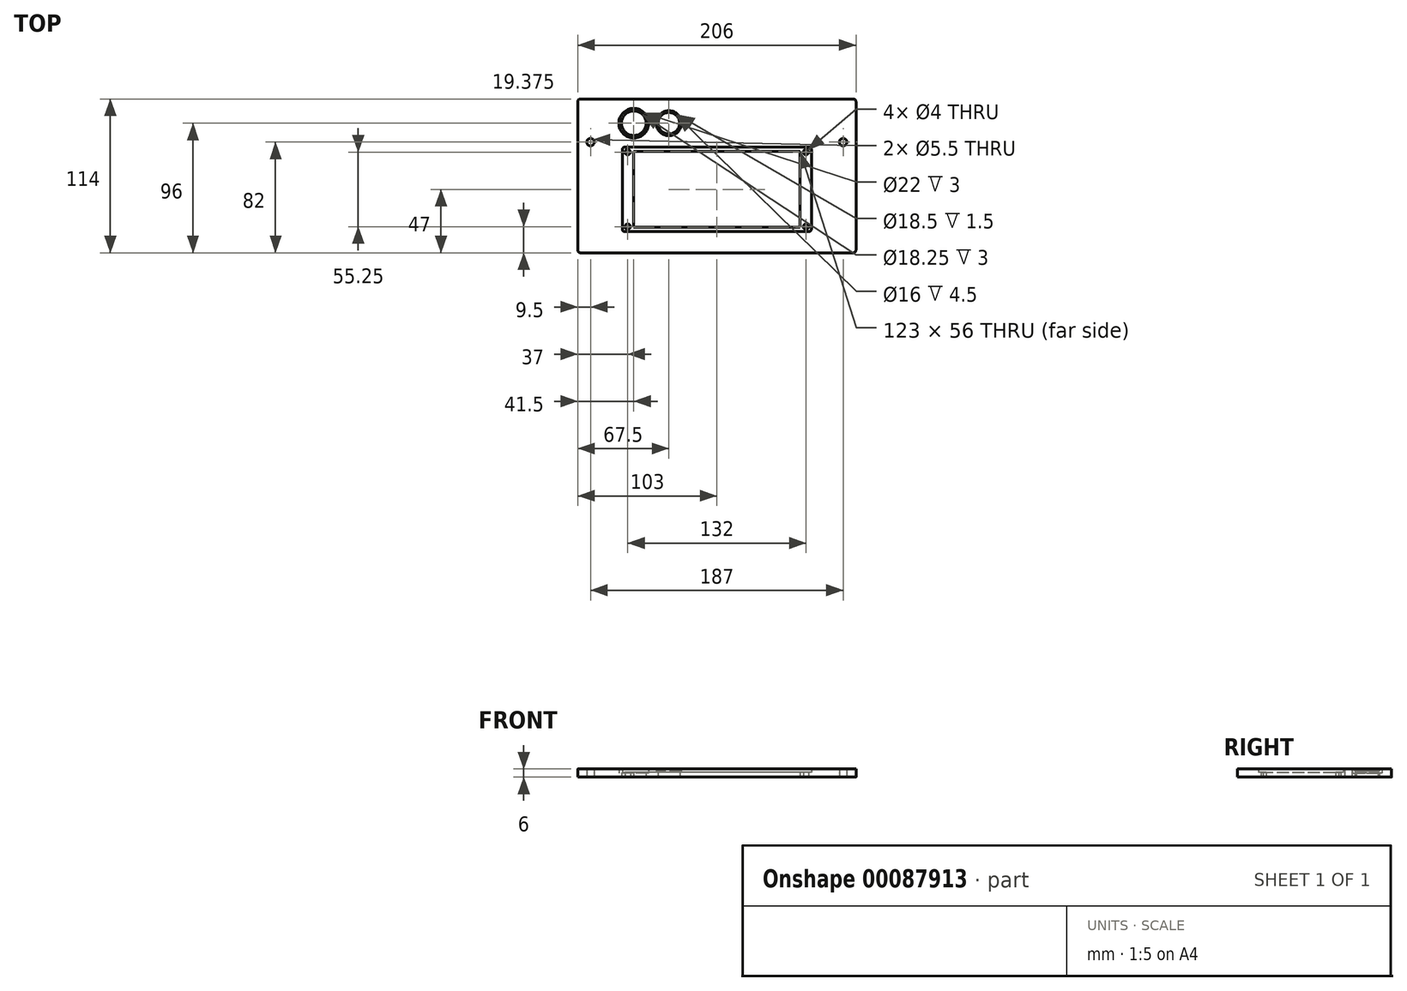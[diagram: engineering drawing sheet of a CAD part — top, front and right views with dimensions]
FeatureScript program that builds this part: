
annotation { "Feature Type Name" : "Feature", "Feature Type Description" : "" }
export const myFeature = defineFeature(function(context is Context, id is Id, definition is map)
    precondition{}
    {
        {
            var Q0;
            Q0=qCreatedBy(makeId("Top.planeOp"),FACE);
            var sketch = newSketch(context, id + "F0", { "sketchPlane" : qUnion([Q0])});
            skLineSegment(sketch, "E0.bottom", {"start": v(101, -57) * mm, "end": v(-101, -57) * mm});
            skLineSegment(sketch, "E0.top", {"start": v(101, 57) * mm, "end": v(-101, 57) * mm});
            skLineSegment(sketch, "E0.left", {"start": v(103, -55) * mm, "end": v(103, 55) * mm});
            skLineSegment(sketch, "E0.right", {"start": v(-103, -55) * mm, "end": v(-103, 55) * mm});
            skPoint(sketch, "E0.middle", {"position": v(0, 0) * mm});
            skPoint(sketch, "E1.visualSharp", {"position": v(-103, 57) * mm});
            skArc(sketch, "E1.filletArc", {"start": v(-101, 57) * mm, "mid": v(-102.41, 56.41) * mm, "end": v(-103, 55) * mm});
            skPoint(sketch, "E2.visualSharp", {"position": v(-103, -57) * mm});
            skArc(sketch, "E2.filletArc", {"start": v(-103, -55) * mm, "mid": v(-102.41, -56.41) * mm, "end": v(-101, -57) * mm});
            skPoint(sketch, "E3.visualSharp", {"position": v(103, -57) * mm});
            skArc(sketch, "E3.filletArc", {"start": v(101, -57) * mm, "mid": v(102.41, -56.41) * mm, "end": v(103, -55) * mm});
            skPoint(sketch, "E4.visualSharp", {"position": v(103, 57) * mm});
            skArc(sketch, "E4.filletArc", {"start": v(103, 55) * mm, "mid": v(102.41, 56.41) * mm, "end": v(101, 57) * mm});
            skLineSegment(sketch, "E5", {"start": v(0, 57) * mm, "end": v(0, 25) * mm, "construction": true});
            skLineSegment(sketch, "E6", {"start": v(0, 25) * mm, "end": v(93.5, 25) * mm, "construction": true});
            skCircle(sketch, "E7", {"center": v(93.5, 25) * mm, "radius": 2.75 * mm});
            skLineSegment(sketch, "E8", {"start": v(0, -57) * mm, "end": v(35.25, -57) * mm});
            skLineSegment(sketch, "E9.bottom", {"start": v(35.25, -57) * mm, "end": v(41.75, -57) * mm});
            skLineSegment(sketch, "E9.top", {"start": v(36.25, -60) * mm, "end": v(40.75, -60) * mm});
            skLineSegment(sketch, "E9.left", {"start": v(35.25, -57) * mm, "end": v(35.25, -59) * mm});
            skLineSegment(sketch, "E9.right", {"start": v(41.75, -57) * mm, "end": v(41.75, -59) * mm});
            skLineSegment(sketch, "E10", {"start": v(0, -10) * mm, "end": v(0, 0) * mm, "construction": true});
            skLineSegment(sketch, "E11.bottom", {"start": v(68, -41.38) * mm, "end": v(-68, -41.38) * mm});
            skLineSegment(sketch, "E11.top", {"start": v(68, 21.37) * mm, "end": v(-68, 21.37) * mm});
            skLineSegment(sketch, "E11.left", {"start": v(70, -39.38) * mm, "end": v(70, 19.37) * mm});
            skLineSegment(sketch, "E11.right", {"start": v(-70, -39.38) * mm, "end": v(-70, 19.37) * mm});
            skPoint(sketch, "E11.middle", {"position": v(0, -10) * mm});
            skPoint(sketch, "E12.visualSharp", {"position": v(-70, 21.37) * mm});
            skArc(sketch, "E12.filletArc", {"start": v(-68, 21.37) * mm, "mid": v(-69.41, 20.79) * mm, "end": v(-70, 19.37) * mm});
            skPoint(sketch, "E13.visualSharp", {"position": v(-70, -41.38) * mm});
            skArc(sketch, "E13.filletArc", {"start": v(-70, -39.38) * mm, "mid": v(-69.41, -40.79) * mm, "end": v(-68, -41.38) * mm});
            skPoint(sketch, "E14.visualSharp", {"position": v(70, -41.38) * mm});
            skArc(sketch, "E14.filletArc", {"start": v(68, -41.38) * mm, "mid": v(69.41, -40.79) * mm, "end": v(70, -39.38) * mm});
            skPoint(sketch, "E15.visualSharp", {"position": v(70, 21.38) * mm});
            skArc(sketch, "E15.filletArc", {"start": v(70, 19.37) * mm, "mid": v(69.41, 20.79) * mm, "end": v(68, 21.37) * mm});
            skPoint(sketch, "E16.visualSharp", {"position": v(35.25, -60) * mm});
            skArc(sketch, "E16.filletArc", {"start": v(35.25, -59) * mm, "mid": v(35.54, -59.7) * mm, "end": v(36.25, -60) * mm});
            skPoint(sketch, "E17.visualSharp", {"position": v(41.75, -60) * mm});
            skArc(sketch, "E17.filletArc", {"start": v(40.75, -60) * mm, "mid": v(41.46, -59.7) * mm, "end": v(41.75, -59) * mm});
            skCircle(sketch, "E18.MirrorC", {"center": v(-93.5, 25) * mm, "radius": 2.75 * mm});
            skLineSegment(sketch, "E19", {"start": v(66, 21.37) * mm, "end": v(66, 17.62) * mm, "construction": true});
            skLineSegment(sketch, "E20", {"start": v(66, 17.62) * mm, "end": v(0, 17.62) * mm, "construction": true});
            skCircle(sketch, "E21", {"center": v(66, 17.62) * mm, "radius": 2 * mm});
            skCircle(sketch, "E22.MirrorC", {"center": v(-66, 17.62) * mm, "radius": 2 * mm});
            skLineSegment(sketch, "E23", {"start": v(66, -41.38) * mm, "end": v(66, -37.63) * mm, "construction": true});
            skLineSegment(sketch, "E24", {"start": v(66, -37.63) * mm, "end": v(0, -37.63) * mm, "construction": true});
            skCircle(sketch, "E25", {"center": v(66, -37.63) * mm, "radius": 2 * mm});
            skCircle(sketch, "E26.MirrorC", {"center": v(-66, -37.63) * mm, "radius": 2 * mm});
            skLineSegment(sketch, "E27.MirrorCS", {"start": v(-35.25, -57) * mm, "end": v(-41.75, -57) * mm});
            skLineSegment(sketch, "E28.MirrorCS", {"start": v(-35.25, -57) * mm, "end": v(-35.25, -59) * mm});
            skArc(sketch, "E29.MirrorCS", {"start": v(-35.25, -59) * mm, "mid": v(-35.54, -59.7) * mm, "end": v(-36.25, -60) * mm});
            skLineSegment(sketch, "E30.MirrorCS", {"start": v(-36.25, -60) * mm, "end": v(-40.75, -60) * mm});
            skArc(sketch, "E31.MirrorCS", {"start": v(-40.75, -60) * mm, "mid": v(-41.46, -59.7) * mm, "end": v(-41.75, -59) * mm});
            skLineSegment(sketch, "E32.MirrorCS", {"start": v(-41.75, -57) * mm, "end": v(-41.75, -59) * mm});
            skLineSegment(sketch, "E33.bottom", {"start": v(61.5, -38) * mm, "end": v(-61.5, -38) * mm});
            skLineSegment(sketch, "E33.top", {"start": v(61.5, 18) * mm, "end": v(-61.5, 18) * mm});
            skLineSegment(sketch, "E33.left", {"start": v(61.5, -38) * mm, "end": v(61.5, 18) * mm});
            skLineSegment(sketch, "E33.right", {"start": v(-61.5, -38) * mm, "end": v(-61.5, 18) * mm});
            skLineSegment(sketch, "E34", {"start": v(-61.5, 18) * mm, "end": v(-61.5, 39) * mm, "construction": true});
            skCircle(sketch, "E35", {"center": v(-61.5, 39) * mm, "radius": 9.12 * mm});
            skLineSegment(sketch, "E36", {"start": v(-61.5, 39) * mm, "end": v(-35.5, 39) * mm, "construction": true});
            skCircle(sketch, "E37", {"center": v(-35.5, 39) * mm, "radius": 8 * mm});
            skCircle(sketch, "E38", {"center": v(-61.5, 39) * mm, "radius": 11 * mm});
            skCircle(sketch, "E39", {"center": v(-35.5, 39) * mm, "radius": 9.25 * mm});
            skSolve(sketch);
        }
        {
            var Q0;
            Q0=makeQuery(id+"F0.imprint","IMPRINT",FACE,{"disambiguationData":[TD([[makeQuery(id+"F0.imprint","IMPRINT",EDGE,{"derivedFrom":sQuery(id+"F0.wireOp",EDGE,"E0.top")}),1.0]])]});
            var Q1;
            Q1=makeQuery(id+"F0.imprint","IMPRINT",FACE,{"disambiguationData":[TD([[makeQuery(id+"F0.imprint","IMPRINT",EDGE,{"derivedFrom":sQuery(id+"F0.wireOp",EDGE,"E27.MirrorCS")}),1.0]])]});
            var Q2;
            Q2=makeQuery(id+"F0.imprint","IMPRINT",FACE,{"disambiguationData":[TD([[makeQuery(id+"F0.imprint","IMPRINT",EDGE,{"derivedFrom":sQuery(id+"F0.wireOp",EDGE,"E9.bottom")}),-1.0]])]});
            extrude(context, id + "F1", {"entities" : qUnion([Q0, Q1, Q2]), "depth" : 6 * mm});
        }
        {
            var Q0;
            Q0=makeQuery(id+"F0.imprint","IMPRINT",FACE,{"disambiguationData":[TD([[makeQuery(id+"F0.imprint","IMPRINT",EDGE,{"derivedFrom":sQuery(id+"F0.wireOp",EDGE,"E11.bottom")}),-1.0]])]});
            extrude(context, id + "F2", {"entities" : qUnion([Q0]), "operationType" : NewBodyOperationType.ADD, "depth" : 3.5 * mm});
        }
        {
            var Q0;
            Q0=makeQuery(id+"F0.imprint","IMPRINT",FACE,{"disambiguationData":[TD([[makeQuery(id+"F0.imprint","IMPRINT",EDGE,{"derivedFrom":sQuery(id+"F0.wireOp",EDGE,"E35")}),-1.0]])]});
            extrude(context, id + "F3", {"entities" : qUnion([Q0]), "operationType" : NewBodyOperationType.ADD, "depth" : 3 * mm});
        }
        {
            var Q0;
            Q0=makeQuery(id+"F0.imprint","IMPRINT",FACE,{"disambiguationData":[TD([[makeQuery(id+"F0.imprint","IMPRINT",EDGE,{"derivedFrom":sQuery(id+"F0.wireOp",EDGE,"E37")}),-1.0]])]});
            extrude(context, id + "F4", {"entities" : qUnion([Q0]), "operationType" : NewBodyOperationType.ADD, "depth" : 4.5 * mm});
        }
    });
